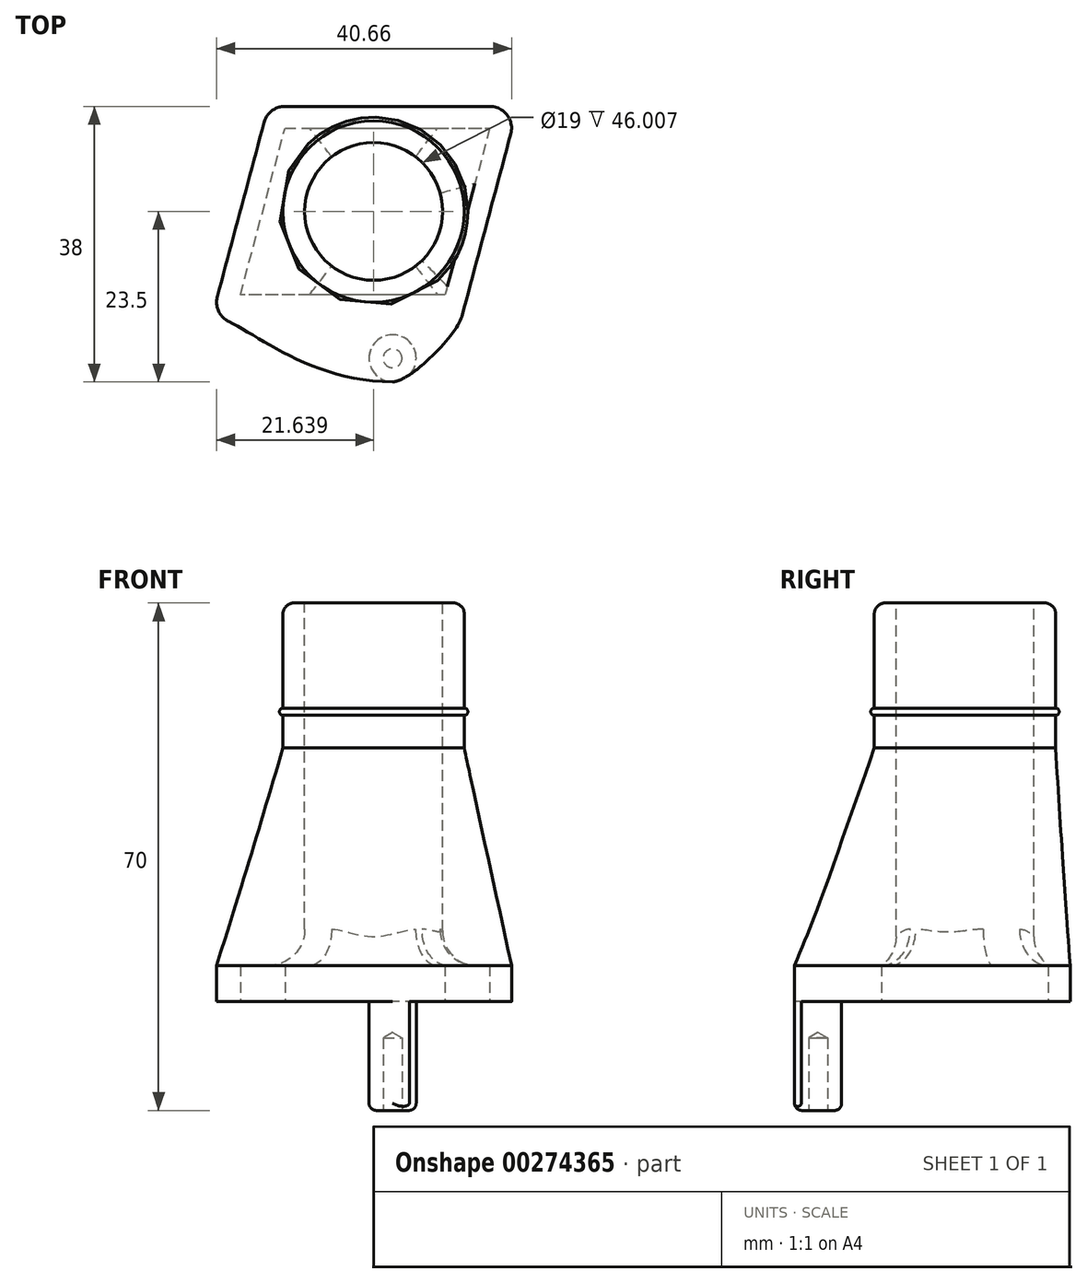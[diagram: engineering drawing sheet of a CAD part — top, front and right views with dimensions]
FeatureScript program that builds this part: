
annotation { "Feature Type Name" : "Feature", "Feature Type Description" : "" }
export const myFeature = defineFeature(function(context is Context, id is Id, definition is map)
    precondition{}
    {
        {
            var Q0;
            Q0=qCreatedBy(makeId("Top.planeOp"),FACE);
            var sketch = newSketch(context, id + "F0", { "sketchPlane" : qUnion([Q0])});
            skLineSegment(sketch, "E0", {"start": v(0, 22) * mm, "end": v(27.2, 22) * mm});
            skLineSegment(sketch, "E1", {"start": v(27.2, 22) * mm, "end": v(21.3, 0) * mm});
            skLineSegment(sketch, "E2", {"start": v(21.3, 0) * mm, "end": v(-5.9, 0) * mm});
            skLineSegment(sketch, "E3", {"start": v(-5.9, 0) * mm, "end": v(0, 22) * mm});
            skPoint(sketch, "E4", {"position": v(0, 0) * mm});
            skLineSegment(sketch, "E5", {"start": v(0, 22) * mm, "end": v(0, 0) * mm, "construction": true});
            skCircle(sketch, "E6", {"center": v(14.45, -9.25) * mm, "radius": 3.25 * mm});
            skLineSegment(sketch, "E7", {"start": v(27.2, 36.46) * mm, "end": v(27.2, -27.15) * mm, "construction": true});
            skLineSegment(sketch, "E8.0", {"start": v(-0.38, 22.5) * mm, "end": v(27.85, 22.5) * mm});
            skLineSegment(sketch, "E8.1", {"start": v(-6.55, -0.5) * mm, "end": v(-0.38, 22.5) * mm});
            skLineSegment(sketch, "E8.2", {"start": v(21.69, -0.5) * mm, "end": v(-6.55, -0.5) * mm});
            skLineSegment(sketch, "E8.3", {"start": v(27.85, 22.5) * mm, "end": v(21.69, -0.5) * mm});
            skLineSegment(sketch, "E9.0", {"start": v(-2.69, 25.5) * mm, "end": v(31.76, 25.5) * mm});
            skLineSegment(sketch, "E9.1", {"start": v(-10.46, -3.5) * mm, "end": v(-2.69, 25.5) * mm});
            skLineSegment(sketch, "E9.2", {"start": v(24, -3.5) * mm, "end": v(-10.46, -3.5) * mm});
            skLineSegment(sketch, "E9.3", {"start": v(31.76, 25.5) * mm, "end": v(24, -3.5) * mm});
            skFitSpline(sketch, "E10", {"points": [v(-10.46, -3.5) * mm, v(14.45, -12.5) * mm], "startDerivative": vector(11.46, 0) * mm, "endDerivative": vector(39.15, 0) * mm});
            skFitSpline(sketch, "E11", {"points": [v(14.45, -12.5) * mm, v(24, -3.5) * mm], "startDerivative": vector(7.59, 0) * mm, "endDerivative": vector(1.96, 7.33) * mm});
            skPoint(sketch, "E12", {"position": v(11.83, 11) * mm});
            skSolve(sketch);
        }
        {
            var Q0;
            Q0=makeQuery(id+"F0.imprint","IMPRINT",FACE,{"disambiguationData":[TD([[makeQuery(id+"F0.imprint","IMPRINT",EDGE,{"derivedFrom":sQuery(id+"F0.wireOp",EDGE,"E8.0")}),1.0]])]});
            var Q1;
            Q1=makeQuery(id+"F0.imprint","IMPRINT",FACE,{"disambiguationData":[TD([[makeQuery(id+"F0.imprint","IMPRINT",EDGE,{"derivedFrom":sQuery(id+"F0.wireOp",EDGE,"E9.2")}),1.0]])]});
            var Q2;
            {var subQ0=sQuery(id+"F0.wireOp",EDGE,"E6");var subQ1=makeQuery(id+"F0.imprint","INTERSECT",VERTEX,{"derivedFrom":[subQ0,sQuery(id+"F0.wireOp",EDGE,"E10")]});Q2=makeQuery(id+"F0.imprint","IMPRINT",FACE,{"disambiguationData":[TD([[makeQuery(id+"F0.imprint","IMPRINT",EDGE,{"disambiguationData":[TD([[subQ1,1.0]])],"derivedFrom":subQ0}),1.0]])]});}
            var Q3;
            Q3=makeQuery(id+"F0.imprint","IMPRINT",FACE,{"disambiguationData":[TD([[makeQuery(id+"F0.imprint","IMPRINT",EDGE,{"derivedFrom":sQuery(id+"F0.wireOp",EDGE,"E0")}),-1.0]])]});
            var Q4;
            Q4=makeQuery(id+"F0.imprint","IMPRINT",FACE,{"disambiguationData":[TD([[makeQuery(id+"F0.imprint","IMPRINT",EDGE,{"derivedFrom":sQuery(id+"F0.wireOp",EDGE,"E0")}),1.0]])]});
            extrude(context, id + "F1", {"entities" : qUnion([Q0, Q1, Q2, Q3, Q4]), "depth" : 5 * mm});
        }
        {
            var Q0;
            {var subQ0=sQuery(id+"F0.wireOp",EDGE,"E6");var subQ1=makeQuery(id+"F0.imprint","INTERSECT",VERTEX,{"derivedFrom":[subQ0,sQuery(id+"F0.wireOp",EDGE,"E10")]});Q0=makeQuery(id+"F0.imprint","IMPRINT",FACE,{"disambiguationData":[TD([[makeQuery(id+"F0.imprint","IMPRINT",EDGE,{"disambiguationData":[TD([[subQ1,1.0]])],"derivedFrom":subQ0}),1.0]])]});}
            extrude(context, id + "F2", {"entities" : qUnion([Q0]), "operationType" : NewBodyOperationType.ADD, "oppositeDirection" : true, "depth" : 15 * mm});
        }
        {
            var Q0;
            Q0=makeQuery(id+"F2.opExtrude","CAP_FACE",FACE,{"disambiguationData":[OSD([sQuery(id+"F0.wireOp",EDGE,"E6")])],"isStart":false});
            var sketch = newSketch(context, id + "F3", { "sketchPlane" : qUnion([Q0])});
            skPoint(sketch, "E13.0", {"position": v(14.45, 9.25) * mm});
            skSolve(sketch);
        }
        {
            var Q0;
            Q0=makeQuery(id+"F2.opExtrude","CAP_EDGE",EDGE,{"disambiguationData":[OSD([sQuery(id+"F0.wireOp",EDGE,"E6")])],"isStart":false});
            fillet(context, id + "F4", {"entities" : qUnion([Q0]), "radius" : 1 * mm, "allowEdgeOverflow" : false});
        }
        {
            var Q0;
            Q0=sQuery(id+"F3.wireOp",VERTEX,"E13.0");
            var Q1;
            Q1=makeQuery(id+"F1.opExtrude","SWEPT_BODY",BODY,{"disambiguationData":[OSD([sQuery(id+"F0.wireOp",EDGE,"E6"),sQuery(id+"F0.wireOp",EDGE,"E8.0"),sQuery(id+"F0.wireOp",EDGE,"E8.1"),sQuery(id+"F0.wireOp",EDGE,"E8.2"),sQuery(id+"F0.wireOp",EDGE,"E8.3"),sQuery(id+"F0.wireOp",EDGE,"E9.0"),sQuery(id+"F0.wireOp",EDGE,"E9.1"),sQuery(id+"F0.wireOp",EDGE,"E9.3"),sQuery(id+"F0.wireOp",EDGE,"E10"),sQuery(id+"F0.wireOp",EDGE,"E11")])]});
            hole(context, id + "F5", {"style" : HoleStyle.SIMPLE, "endStyle" : HoleEndStyle.BLIND, "holeDiameter" : 2.6 * mm, "holeDepth" : 10 * mm, "tappedDepth" : 12 * mm, "tapClearance" : 3, "locations" : qUnion([Q0]), "scope" : qUnion([Q1])});
        }
        {
            var Q0;
            Q0=makeQuery(id+"F1.opExtrude","CAP_FACE",FACE,{"disambiguationData":[OSD([sQuery(id+"F0.wireOp",EDGE,"E6"),sQuery(id+"F0.wireOp",EDGE,"E8.0"),sQuery(id+"F0.wireOp",EDGE,"E8.1"),sQuery(id+"F0.wireOp",EDGE,"E8.2"),sQuery(id+"F0.wireOp",EDGE,"E8.3"),sQuery(id+"F0.wireOp",EDGE,"E9.0"),sQuery(id+"F0.wireOp",EDGE,"E9.1"),sQuery(id+"F0.wireOp",EDGE,"E9.3"),sQuery(id+"F0.wireOp",EDGE,"E10"),sQuery(id+"F0.wireOp",EDGE,"E11")])],"isStart":false});
            cPlane(context, id + "F6", {"entities" : qUnion([Q0]), "cplaneType" : CPlaneType.OFFSET, "offset" : 30 * mm, "width" : 150 * mm, "height" : 150 * mm});
        }
        {
            var Q0;
            Q0=qCreatedBy(id+"F6.planeOp",FACE);
            var sketch = newSketch(context, id + "F7", { "sketchPlane" : qUnion([Q0])});
            skCircle(sketch, "E14", {"center": v(11.83, 11) * mm, "radius": 12.5 * mm});
            skCircle(sketch, "E15.0", {"center": v(11.83, 11) * mm, "radius": 9.5 * mm});
            skSolve(sketch);
        }
        {
            var Q0;
            Q0=makeQuery(id+"F7.imprint","IMPRINT",FACE,{"disambiguationData":[TD([[makeQuery(id+"F7.imprint","IMPRINT",EDGE,{"derivedFrom":sQuery(id+"F7.wireOp",EDGE,"E14")}),1.0]])]});
            var Q1;
            Q1=makeQuery(id+"F7.imprint","IMPRINT",FACE,{"disambiguationData":[TD([[makeQuery(id+"F7.imprint","IMPRINT",EDGE,{"derivedFrom":sQuery(id+"F7.wireOp",EDGE,"E15.0")}),1.0]])]});
            extrude(context, id + "F8", {"entities" : qUnion([Q0, Q1]), "depth" : 20 * mm});
        }
        {
            var Q0;
            Q0=makeQuery(id+"F1.opExtrude","SWEPT_EDGE",EDGE,{"disambiguationData":[OSD([sQuery(id+"F0.wireOp",EDGE,"E9.0"),sQuery(id+"F0.wireOp",EDGE,"E9.3")])]});
            var Q1;
            Q1=makeQuery(id+"F1.opExtrude","SWEPT_EDGE",EDGE,{"disambiguationData":[OSD([sQuery(id+"F0.wireOp",EDGE,"E9.0"),sQuery(id+"F0.wireOp",EDGE,"E9.1")])]});
            var Q2;
            Q2=makeQuery(id+"F1.opExtrude","SWEPT_EDGE",EDGE,{"disambiguationData":[OSD([sQuery(id+"F0.wireOp",EDGE,"E9.1"),sQuery(id+"F0.wireOp",EDGE,"E9.2"),sQuery(id+"F0.wireOp",EDGE,"E10")])]});
            fillet(context, id + "F9", {"entities" : qUnion([Q0, Q1, Q2]), "radius" : 3 * mm, "tangentPropagation" : true, "allowEdgeOverflow" : false});
        }
        {
            var Q0;
            Q0=makeQuery(id+"F1.opExtrude","CAP_FACE",FACE,{"disambiguationData":[OSD([sQuery(id+"F0.wireOp",EDGE,"E6"),sQuery(id+"F0.wireOp",EDGE,"E9.0"),sQuery(id+"F0.wireOp",EDGE,"E9.1"),sQuery(id+"F0.wireOp",EDGE,"E9.3"),sQuery(id+"F0.wireOp",EDGE,"E10"),sQuery(id+"F0.wireOp",EDGE,"E11")])],"isStart":false});
            var Q1;
            Q1=makeQuery(id+"F8.opExtrude","CAP_FACE",FACE,{"disambiguationData":[OSD([sQuery(id+"F7.wireOp",EDGE,"E14")])],"isStart":true});
            loft(context, id + "F10", {"operationType" : NewBodyOperationType.ADD, "sheetProfilesArray" : [{ "sheetProfileEntities" : qUnion([Q0]) }, { "sheetProfileEntities" : qUnion([Q1]) }]});
        }
        {
            var Q0;
            Q0=makeQuery(id+"F0.imprint","IMPRINT",FACE,{"disambiguationData":[TD([[makeQuery(id+"F0.imprint","IMPRINT",EDGE,{"derivedFrom":sQuery(id+"F0.wireOp",EDGE,"E0")}),-1.0]])]});
            var Q1;
            Q1=makeQuery(id+"F0.imprint","IMPRINT",FACE,{"disambiguationData":[TD([[makeQuery(id+"F0.imprint","IMPRINT",EDGE,{"derivedFrom":sQuery(id+"F0.wireOp",EDGE,"E0")}),1.0]])]});
            var Q2;
            Q2=makeQuery(id+"F10.opLoft","SWEPT_FACE",FACE,{"disambiguationData":[OSD([sQuery(id+"F0.wireOp",EDGE,"E6"),sQuery(id+"F0.wireOp",EDGE,"E9.0"),sQuery(id+"F0.wireOp",EDGE,"E9.1"),sQuery(id+"F0.wireOp",EDGE,"E9.2"),sQuery(id+"F0.wireOp",EDGE,"E10"),sQuery(id+"F7.wireOp",EDGE,"E14")])]});
            extrude(context, id + "F11", {"entities" : qUnion([Q0, Q1]), "operationType" : NewBodyOperationType.REMOVE, "endBoundEntityFace" : qUnion([Q2]), "depth" : 5 * mm});
        }
        {
            var Q0;
            Q0=makeQuery(id+"F8.opExtrude","CAP_EDGE",EDGE,{"disambiguationData":[OSD([sQuery(id+"F7.wireOp",EDGE,"E14")])],"isStart":false});
            fillet(context, id + "F12", {"entities" : qUnion([Q0]), "radius" : 1.5 * mm, "tangentPropagation" : true, "allowEdgeOverflow" : false});
        }
        {
            var Q0;
            Q0=qCreatedBy(id+"F6.planeOp",FACE);
            cPlane(context, id + "F13", {"entities" : qUnion([Q0]), "cplaneType" : CPlaneType.OFFSET, "offset" : 5 * mm, "width" : 150 * mm, "height" : 150 * mm});
        }
        {
            var Q0;
            Q0=qCreatedBy(id+"F13.planeOp",FACE);
            var sketch = newSketch(context, id + "F14", { "sketchPlane" : qUnion([Q0])});
            skCircle(sketch, "E16", {"center": v(11.83, 11) * mm, "radius": 13 * mm});
            skSolve(sketch);
        }
        {
            var Q0;
            Q0 = qSketchRegion(id + "F14", true);
            var Q1;
            Q1=makeQuery(id+"F14.imprint","IMPRINT",FACE,{"disambiguationData":[TD([[makeQuery(id+"F14.imprint","IMPRINT",EDGE,{"derivedFrom":sQuery(id+"F14.wireOp",EDGE,"E16")}),1.0]])]});
            extrude(context, id + "F15", {"entities" : qUnion([Q0, Q1]), "operationType" : NewBodyOperationType.ADD, "endBound" : BoundingType.SYMMETRIC, "depth" : 1 * mm});
        }
        {
            var Q0;
            Q0=makeQuery(id+"F7.imprint","IMPRINT",FACE,{"disambiguationData":[TD([[makeQuery(id+"F7.imprint","IMPRINT",EDGE,{"derivedFrom":sQuery(id+"F7.wireOp",EDGE,"E15.0")}),1.0]])]});
            extrude(context, id + "F16", {"entities" : qUnion([Q0]), "operationType" : NewBodyOperationType.REMOVE, "endBound" : BoundingType.SYMMETRIC, "oppositeDirection" : true, "depth" : 200 * mm});
        }
        {
            var Q0;
            Q0=makeQuery(id+"F16.boolean.opBoolean","INTERSECT",EDGE,{"derivedFrom":[makeQuery(id+"F11.boolean.opBoolean","COPY",FACE,{"derivedFrom":makeQuery(id+"F11.opExtrude","CAP_FACE",FACE,{"disambiguationData":[OSD([sQuery(id+"F0.wireOp",EDGE,"E8.0"),sQuery(id+"F0.wireOp",EDGE,"E8.1"),sQuery(id+"F0.wireOp",EDGE,"E8.2"),sQuery(id+"F0.wireOp",EDGE,"E8.3")])],"isStart":false})}),makeQuery(id+"F16.opExtrude","SWEPT_FACE",FACE,{"disambiguationData":[OSD([sQuery(id+"F7.wireOp",EDGE,"E15.0")])]})]});
            fillet(context, id + "F17", {"entities" : qUnion([Q0]), "radius" : 5 * mm, "tangentPropagation" : true, "allowEdgeOverflow" : false});
        }
        {
            var Q0;
            Q0=makeQuery(id+"F15.opExtrude","CAP_EDGE",EDGE,{"disambiguationData":[OSD([sQuery(id+"F14.wireOp",EDGE,"E16")])],"isStart":true});
            var Q1;
            Q1=makeQuery(id+"F15.opExtrude","CAP_EDGE",EDGE,{"disambiguationData":[OSD([sQuery(id+"F14.wireOp",EDGE,"E16")])],"isStart":false});
            fillet(context, id + "F18", {"entities" : qUnion([Q0, Q1]), "radius" : 0.5 * mm, "tangentPropagation" : true, "allowEdgeOverflow" : false});
        }
    });
